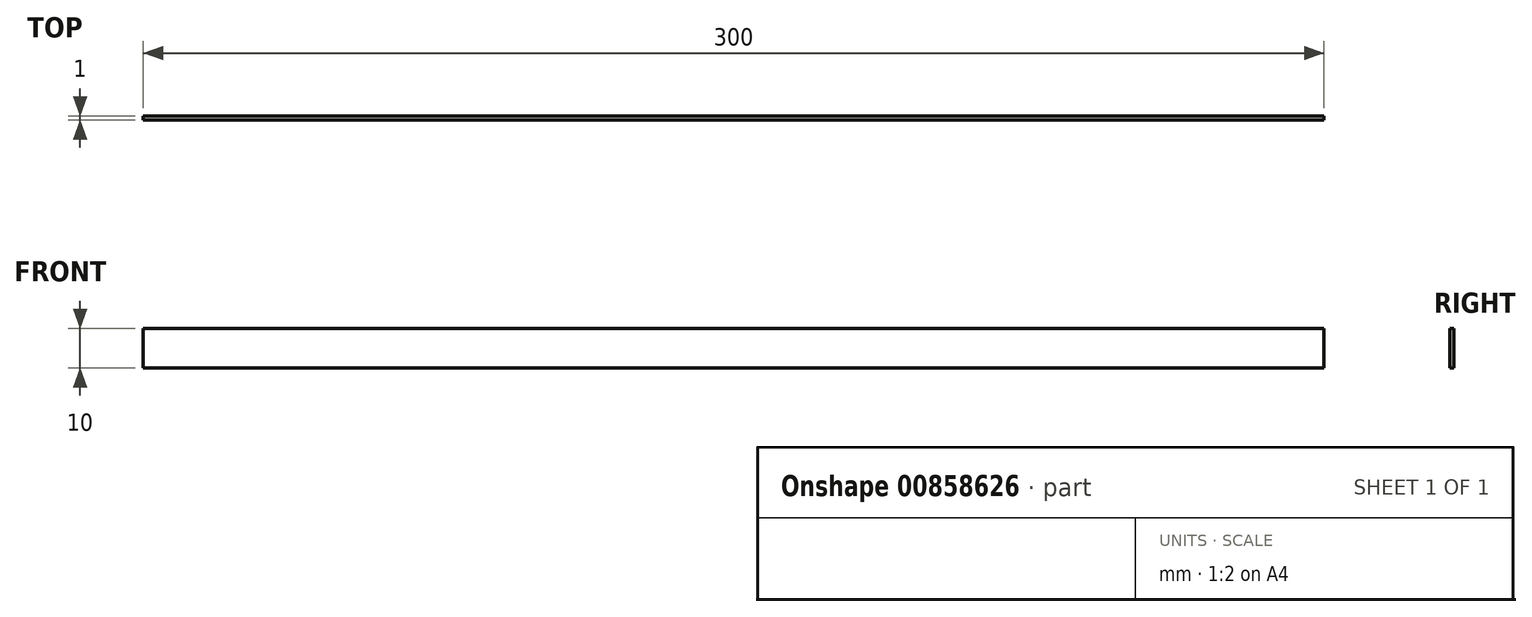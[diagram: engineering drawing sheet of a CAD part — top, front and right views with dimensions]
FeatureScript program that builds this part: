
annotation { "Feature Type Name" : "Feature", "Feature Type Description" : "" }
export const myFeature = defineFeature(function(context is Context, id is Id, definition is map)
    precondition{}
    {
        {
            var Q0;
            Q0=qCreatedBy(makeId("Front.planeOp"),FACE);
            var sketch = newSketch(context, id + "F0", { "sketchPlane" : qUnion([Q0])});
            skLineSegment(sketch, "E0.bottom", {"start": v(0, 0) * mm, "end": v(300, 0) * mm});
            skLineSegment(sketch, "E0.top", {"start": v(0, 10) * mm, "end": v(300, 10) * mm});
            skLineSegment(sketch, "E0.left", {"start": v(0, 0) * mm, "end": v(0, 10) * mm});
            skLineSegment(sketch, "E0.right", {"start": v(300, 0) * mm, "end": v(300, 10) * mm});
            skSolve(sketch);
        }
        {
            var Q0;
            Q0=makeQuery(id+"F0.imprint","IMPRINT",FACE,{"disambiguationData":[TD([[makeQuery(id+"F0.imprint","IMPRINT",EDGE,{"derivedFrom":sQuery(id+"F0.wireOp",EDGE,"E0.bottom")}),1.0]])]});
            extrude(context, id + "F1", {"entities" : qUnion([Q0]), "depth" : 1 * mm, "offsetDistance" : 25 * mm});
        }
    });
